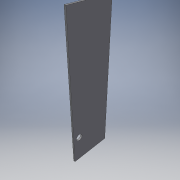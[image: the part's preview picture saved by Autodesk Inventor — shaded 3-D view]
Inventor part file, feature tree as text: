
AUTODESK INVENTOR PART (.ipt)
format: ipt  version: 2016 (Build 200138000, 138)  size: 98,304 bytes
history: native  units: in
note: dims shown in document units (in); Inventor stores cm internally (conversion verified against a paired STEP export)
features: extrude x2, sketch x2
ambient origin geometry x8: Origin, YZ Plane, XZ Plane, XY Plane, X Axis, Y Axis, Z Axis, Center Point
bodies: Solid1 (feature_tree)
feature tree (4):
  extrude  "Extrusion1"  Depth=18.0in
  extrude  "Extrusion2"  Depth=0.75in
  sketch  "Sketch1"  dims[d0=62.0in d1=18.0in]
  sketch  "Sketch2"  dims[d2=0.75in d3=0.0in d5=3.0in d8=2.8in d9=12.0in d12=1.0in d13=0.0in]
